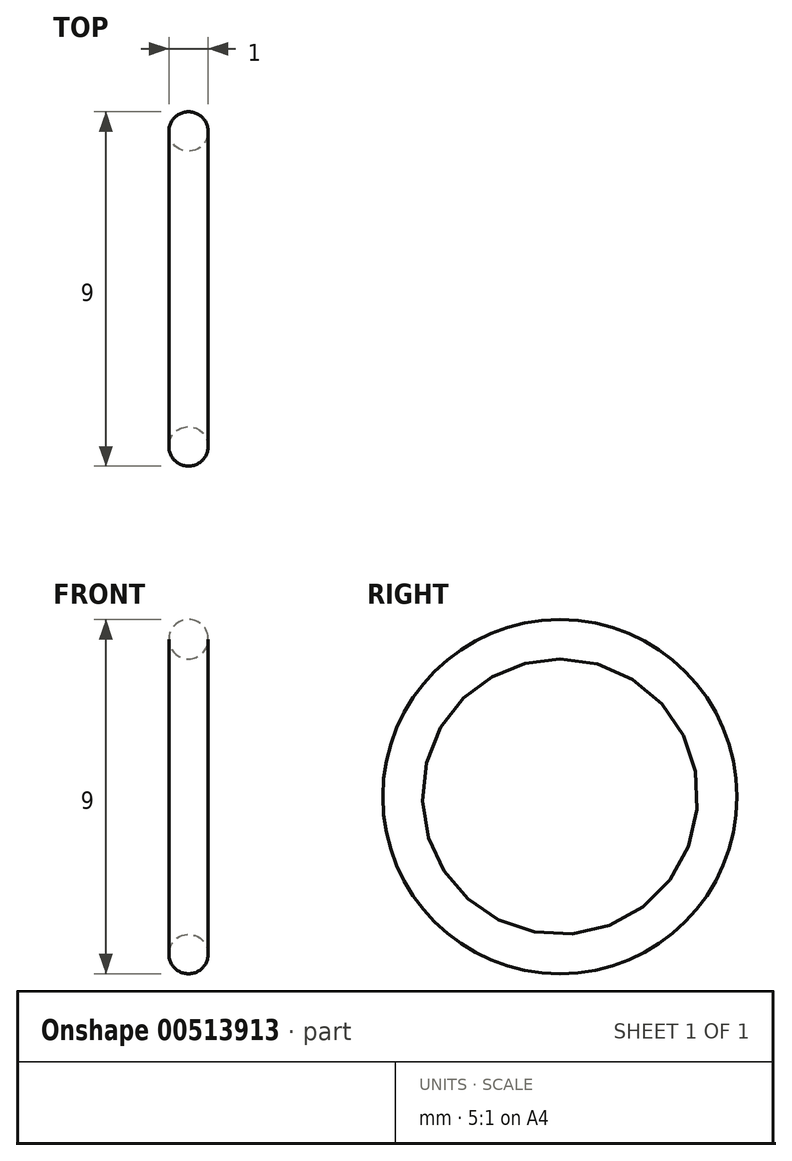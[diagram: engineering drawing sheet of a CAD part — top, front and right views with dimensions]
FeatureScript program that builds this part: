
annotation { "Feature Type Name" : "Feature", "Feature Type Description" : "" }
export const myFeature = defineFeature(function(context is Context, id is Id, definition is map)
    precondition{}
    {
        {
            var Q0;
            Q0=qCreatedBy(makeId("Right.planeOp"),FACE);
            var sketch = newSketch(context, id + "F0", { "sketchPlane" : qUnion([Q0])});
            skCircle(sketch, "E0", {"center": v(0, 0) * mm, "radius": 4 * mm});
            skSolve(sketch);
        }
        {
            var Q0;
            Q0=qCreatedBy(makeId("Top.planeOp"),FACE);
            var sketch = newSketch(context, id + "F1", { "sketchPlane" : qUnion([Q0])});
            skCircle(sketch, "E1", {"center": v(0, 4) * mm, "radius": 0.5 * mm});
            skSolve(sketch);
        }
        {
            var Q0;
            Q0=makeQuery(id+"F1.imprint","IMPRINT",FACE,{"disambiguationData":[TD([[makeQuery(id+"F1.imprint","IMPRINT",EDGE,{"derivedFrom":sQuery(id+"F1.wireOp",EDGE,"E1")}),1.0]])]});
            var Q1;
            Q1=sQuery(id+"F0.wireOp",EDGE,"E0");
            revolve(context, id + "F2", {"entities" : qUnion([Q0]), "axis" : qUnion([Q1]), "revolveType" : RevolveType.FULL});
        }
    });
